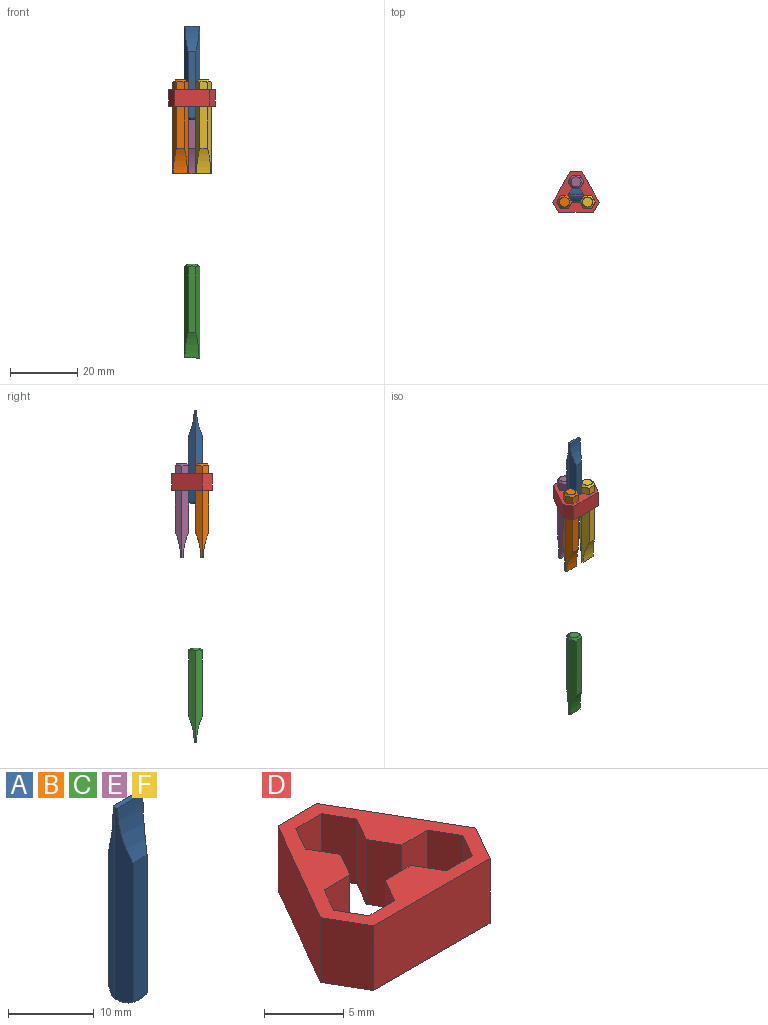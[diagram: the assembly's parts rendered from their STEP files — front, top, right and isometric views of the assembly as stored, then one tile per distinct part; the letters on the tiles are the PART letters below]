
ASSEMBLY  parts=6 mates=7
PART A: 11 faces, bbox 4.6x4.6x28 mm
  f0: plane 20x2.31mm, normal (0,1,0), area 45.9mm2, adj f2,f6,f7,f9
  f1: plane 4.62x0.7mm, normal (0,0,1), area 3.1mm2, adj f2,f3,f5,f6,f7,f8
  f2: plane 27.5x2mm, normal (-0.87,0.5,0), area 53.6mm2, adj f0,f1,f3,f7,f9
  f3: plane 27.5x2mm, normal (-0.87,-0.5,0), area 53.6mm2, adj f1,f2,f4,f8,f9
  f4: plane 20x2.31mm, normal (0,-1,0), area 45.9mm2, adj f3,f5,f8,f9
  f5: plane 27.5x2mm, normal (0.87,-0.5,0), area 53.6mm2, adj f1,f4,f6,f8,f9
  f6: plane 27.5x2mm, normal (0.87,0.5,0), area 53.6mm2, adj f0,f1,f5,f7,f9
  f7: cylinder r=17.87mm len=7.5mm, axis (1,0,0), area 27.7mm2, adj f0,f1,f2,f6
  f8: cylinder r=17.87mm len=7.5mm, axis (1,0,0), area 27.7mm2, adj f1,f3,f4,f5
  f9: cone r=1.5mm half-angle=45deg, axis (0,0,1), area 9.6mm2, adj f0,f2,f3,f4,f5,f6,f10
  f10: plane 3x3mm, normal (0,0,-1), area 7.1mm2, adj f9
PART B: same geometry as A
PART C: same geometry as A
PART D: 26 faces, bbox 13.9x12x5 mm
  f0: plane 5x2mm, normal (-0.87,-0.5,0), area 11.5mm2, adj f1,f23,f24,f25
  f1: plane 5x2.31mm, normal (0,-1,0), area 11.5mm2, adj f0,f2,f24,f25
  f2: plane 5x2mm, normal (-0.87,-0.5,0), area 11.5mm2, adj f1,f3,f24,f25
  f3: plane 5x2mm, normal (-0.87,0.5,0), area 11.5mm2, adj f2,f4,f24,f25
  f4: plane 5x2.31mm, normal (0,1,0), area 11.5mm2, adj f3,f5,f24,f25
  f5: plane 5x2mm, normal (0.87,0.5,0), area 11.5mm2, adj f4,f6,f24,f25
  f6: plane 5x2.31mm, normal (0,1,0), area 11.5mm2, adj f5,f7,f24,f25
  f7: plane 5x2mm, normal (-0.87,0.5,0), area 11.5mm2, adj f6,f8,f24,f25
  f8: plane 5x2.31mm, normal (0,1,0), area 11.5mm2, adj f7,f9,f24,f25
  f9: plane 5x2mm, normal (0.87,0.5,0), area 11.5mm2, adj f8,f10,f24,f25
  f10: plane 5x2mm, normal (0.87,-0.5,0), area 11.5mm2, adj f9,f11,f24,f25
  f11: plane 5x2.31mm, normal (0,-1,0), area 11.5mm2, adj f10,f12,f24,f25
  f12: plane 5x2mm, normal (0.87,-0.5,0), area 11.5mm2, adj f11,f13,f24,f25
  f13: plane 5x2mm, normal (0.87,0.5,0), area 11.5mm2, adj f12,f14,f24,f25
  f14: plane 5x2mm, normal (0.87,-0.5,0), area 11.5mm2, adj f13,f15,f24,f25
  f15: plane 5x2.31mm, normal (0,-1,0), area 11.5mm2, adj f14,f16,f24,f25
  f16: plane 5x2mm, normal (-0.87,-0.5,0), area 11.5mm2, adj f15,f23,f24,f25
  f17: plane 10.39x5mm, normal (0,-1,0), area 52mm2, adj f18,f22,f24,f25
  f18: plane 5x3mm, normal (0.87,-0.5,0), area 17.3mm2, adj f17,f19,f24,f25
  f19: plane 9x5.2mm, normal (0.87,0.5,0), area 52mm2, adj f18,f20,f24,f25
  f20: plane 5x3.46mm, normal (0,1,0), area 17.3mm2, adj f19,f21,f24,f25
  f21: plane 9x5.2mm, normal (-0.87,0.5,0), area 52mm2, adj f20,f22,f24,f25
  f22: plane 5x3mm, normal (-0.87,-0.5,0), area 17.3mm2, adj f17,f21,f24,f25
  f23: plane 5x2mm, normal (-0.87,0.5,0), area 11.5mm2, adj f0,f16,f24,f25
  f24: plane 13.86x12mm, normal (0,0,1), area 58.9mm2, adj f0,f1,f2,f3,f4,f5,f6,f7
  f25: plane 13.86x12mm, normal (0,0,-1), area 58.9mm2, adj f0,f1,f2,f3,f4,f5,f6,f7
PART E: same geometry as A
PART F: same geometry as A
PLACE A rot(axis=(0,0,1),180deg) t=(0,0,-57.51)mm
PLACE B rot(axis=(0,1,0),180deg) t=(-3.46,-2,-45.54)mm
PLACE C rot(axis=(0,-1,0),180deg) t=(0,0,-100.58)mm
PLACE D t=(0,0,-53.46)mm
PLACE E rot(axis=(0,1,0),180deg) t=(0,4,-45.54)mm
PLACE F rot(axis=(0,-1,0),180deg) t=(3.46,-2,-45.54)mm
MATE slider C.f9 <-> A.f9  axis (0,0,1) through (0,0,-100.58)mm
MATE slider C.f9 <-> D.f25  axis (0,0,1) through (0,0,-100.58)mm
MATE slider F.f1 <-> D.f25  axis (0,0,-1) through (5.77,-2,-73.54)mm
MATE planar B.f9 <-> E.f9  axis (0,0,1) through (-3.46,-2,-45.54)mm
MATE slider B.f1 <-> D.f25  axis (0,0,-1) through (-5.77,-2,-73.54)mm
MATE slider E.f1 <-> D.f25  axis (0,0,-1) through (-2.31,4,-73.54)mm
MATE planar F.f9 <-> E.f9  axis (0,0,1) through (3.46,-2,-45.54)mm
